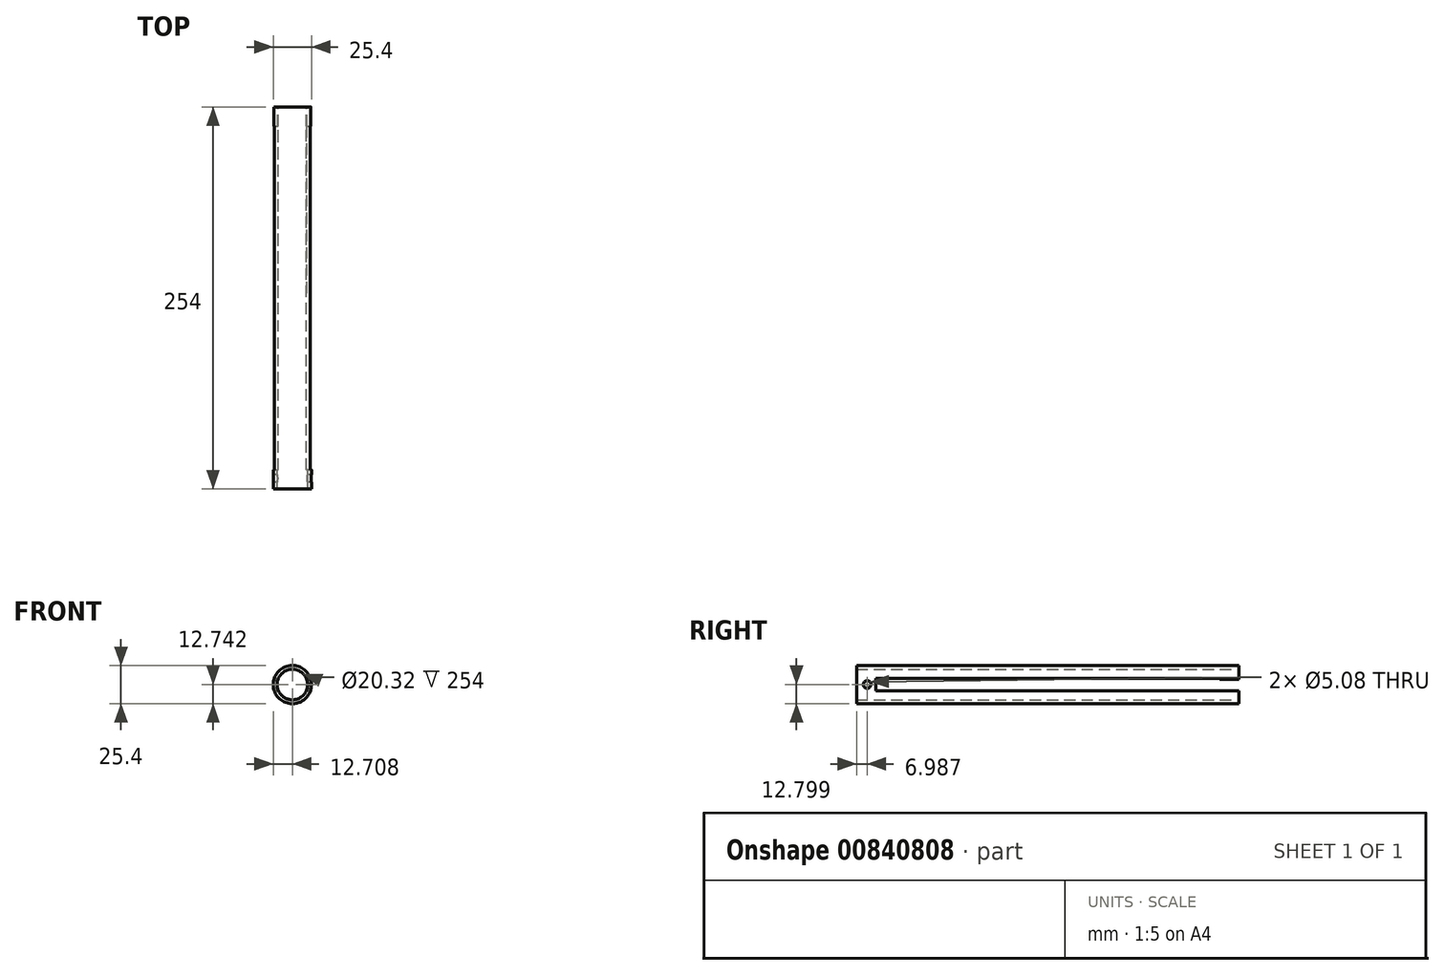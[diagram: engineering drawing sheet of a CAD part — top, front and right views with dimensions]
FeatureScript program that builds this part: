
annotation { "Feature Type Name" : "Feature", "Feature Type Description" : "" }
export const myFeature = defineFeature(function(context is Context, id is Id, definition is map)
    precondition{}
    {
        {
            var Q0;
            Q0=qCreatedBy(makeId("Front.planeOp"),FACE);
            var sketch = newSketch(context, id + "F0", { "sketchPlane" : qUnion([Q0])});
            skCircle(sketch, "E0", {"center": v(-45.2, 26.54) * mm, "radius": 12.7 * mm});
            skPoint(sketch, "E0.first.point", {"position": v(-51.92, 37.32) * mm});
            skPoint(sketch, "E0.second.point", {"position": v(-32.74, 24.08) * mm});
            skPoint(sketch, "E0.third.point", {"position": v(-53, 16.52) * mm});
            skSolve(sketch);
        }
        {
            var Q0;
            Q0 = qSketchRegion(id + "F0", true);
            extrude(context, id + "F1", {"entities" : qUnion([Q0]), "endBound" : BoundingType.SYMMETRIC, "depth" : 254 * mm, "offsetDistance" : 25.4 * mm});
        }
        {
            var Q0;
            Q0=qCreatedBy(makeId("Front.planeOp"),FACE);
            var sketch = newSketch(context, id + "F2", { "sketchPlane" : qUnion([Q0])});
            skCircle(sketch, "E1", {"center": v(-45.2, 26.58) * mm, "radius": 10.16 * mm});
            skPoint(sketch, "E1.first.point", {"position": v(-45.31, 16.42) * mm});
            skPoint(sketch, "E1.second.point", {"position": v(-45.31, 36.74) * mm});
            skPoint(sketch, "E1.third.point", {"position": v(-35.15, 28.14) * mm});
            skSolve(sketch);
        }
        {
            var Q0;
            Q0 = qSketchRegion(id + "F2", true);
            extrude(context, id + "F3", {"entities" : qUnion([Q0]), "operationType" : NewBodyOperationType.REMOVE, "endBound" : BoundingType.SYMMETRIC, "depth" : 254 * mm, "offsetDistance" : 25.4 * mm});
        }
        {
            var Q0;
            Q0=qCreatedBy(makeId("Front.planeOp"),FACE);
            var sketch = newSketch(context, id + "F4", { "sketchPlane" : qUnion([Q0])});
            skLineSegment(sketch, "E2", {"start": v(-45.58, 13.51) * mm, "end": v(-29.8, 13.51) * mm});
            skLineSegment(sketch, "E3", {"start": v(-29.8, 13.51) * mm, "end": v(-45.58, 13.51) * mm});
            skLineSegment(sketch, "E4", {"start": v(-59.92, 13.51) * mm, "end": v(-45.58, 13.51) * mm});
            skLineSegment(sketch, "E5", {"start": v(-45.58, 39.53) * mm, "end": v(-59.3, 39.53) * mm});
            skLineSegment(sketch, "E6", {"start": v(-59.3, 39.53) * mm, "end": v(-45.58, 39.53) * mm});
            skLineSegment(sketch, "E7", {"start": v(-29.8, 39.53) * mm, "end": v(-45.58, 39.53) * mm});
            skLineSegment(sketch, "E8", {"start": v(-59.3, 39.53) * mm, "end": v(-59.3, 30.64) * mm});
            skLineSegment(sketch, "E9", {"start": v(-29.8, 13.51) * mm, "end": v(-29.8, 22.4) * mm});
            skLineSegment(sketch, "E10.bottom", {"start": v(-59.3, 30.64) * mm, "end": v(-29.8, 30.64) * mm});
            skLineSegment(sketch, "E10.top", {"start": v(-59.3, 22.4) * mm, "end": v(-29.8, 22.4) * mm});
            skLineSegment(sketch, "E10.left", {"start": v(-59.3, 30.64) * mm, "end": v(-59.3, 22.4) * mm});
            skLineSegment(sketch, "E10.right", {"start": v(-29.8, 30.64) * mm, "end": v(-29.8, 22.4) * mm});
            skSolve(sketch);
        }
        {
            var Q0;
            Q0=makeQuery(id+"F4.imprint","IMPRINT",FACE,{"disambiguationData":[TD([[makeQuery(id+"F4.imprint","IMPRINT",EDGE,{"derivedFrom":sQuery(id+"F4.wireOp",EDGE,"E10.bottom")}),-1.0]])]});
            var Q1;
            Q1 = qSketchRegion(id + "FKLGw6BRtArWOEl_1", true);
            extrude(context, id + "F5", {"entities" : qUnion([Q0, Q1]), "operationType" : NewBodyOperationType.REMOVE, "endBound" : BoundingType.SYMMETRIC, "depth" : 228.6 * mm, "offsetDistance" : 25.4 * mm});
        }
        {
            var Q0;
            Q0=qCreatedBy(makeId("Front.planeOp"),FACE);
            var sketch = newSketch(context, id + "F6", { "sketchPlane" : qUnion([Q0])});
            skLineSegment(sketch, "E11.bottom", {"start": v(-58.3, 30.03) * mm, "end": v(-31, 30.03) * mm});
            skLineSegment(sketch, "E11.top", {"start": v(-58.3, 22.4) * mm, "end": v(-31, 22.4) * mm});
            skLineSegment(sketch, "E11.left", {"start": v(-58.3, 30.03) * mm, "end": v(-58.3, 22.4) * mm});
            skLineSegment(sketch, "E11.right", {"start": v(-31, 30.03) * mm, "end": v(-31, 22.4) * mm});
            skSolve(sketch);
        }
        {
            var Q0;
            Q0=makeQuery(id+"F6.imprint","IMPRINT",FACE,{"disambiguationData":[TD([[makeQuery(id+"F6.imprint","IMPRINT",EDGE,{"derivedFrom":sQuery(id+"F6.wireOp",EDGE,"E11.bottom")}),-1.0]])]});
            extrude(context, id + "F7", {"entities" : qUnion([Q0]), "operationType" : NewBodyOperationType.REMOVE, "oppositeDirection" : true, "depth" : 228.6 * mm, "offsetDistance" : 25.4 * mm});
        }
        {
            var Q0;
            Q0=qCreatedBy(makeId("Right.planeOp"),FACE);
            var sketch = newSketch(context, id + "F8", { "sketchPlane" : qUnion([Q0])});
            skCircle(sketch, "E12", {"center": v(-120.01, 26.64) * mm, "radius": 2.54 * mm});
            skPoint(sketch, "E12.first.point", {"position": v(-117.94, 28.1) * mm});
            skPoint(sketch, "E12.second.point", {"position": v(-117.96, 25.15) * mm});
            skPoint(sketch, "E12.third.point", {"position": v(-122.55, 26.8) * mm});
            skSolve(sketch);
        }
        {
            var Q0;
            Q0 = qSketchRegion(id + "F8", true);
            extrude(context, id + "F9", {"entities" : qUnion([Q0]), "operationType" : NewBodyOperationType.REMOVE, "endBound" : BoundingType.SYMMETRIC, "depth" : 254 * mm, "offsetDistance" : 25.4 * mm});
        }
    });
